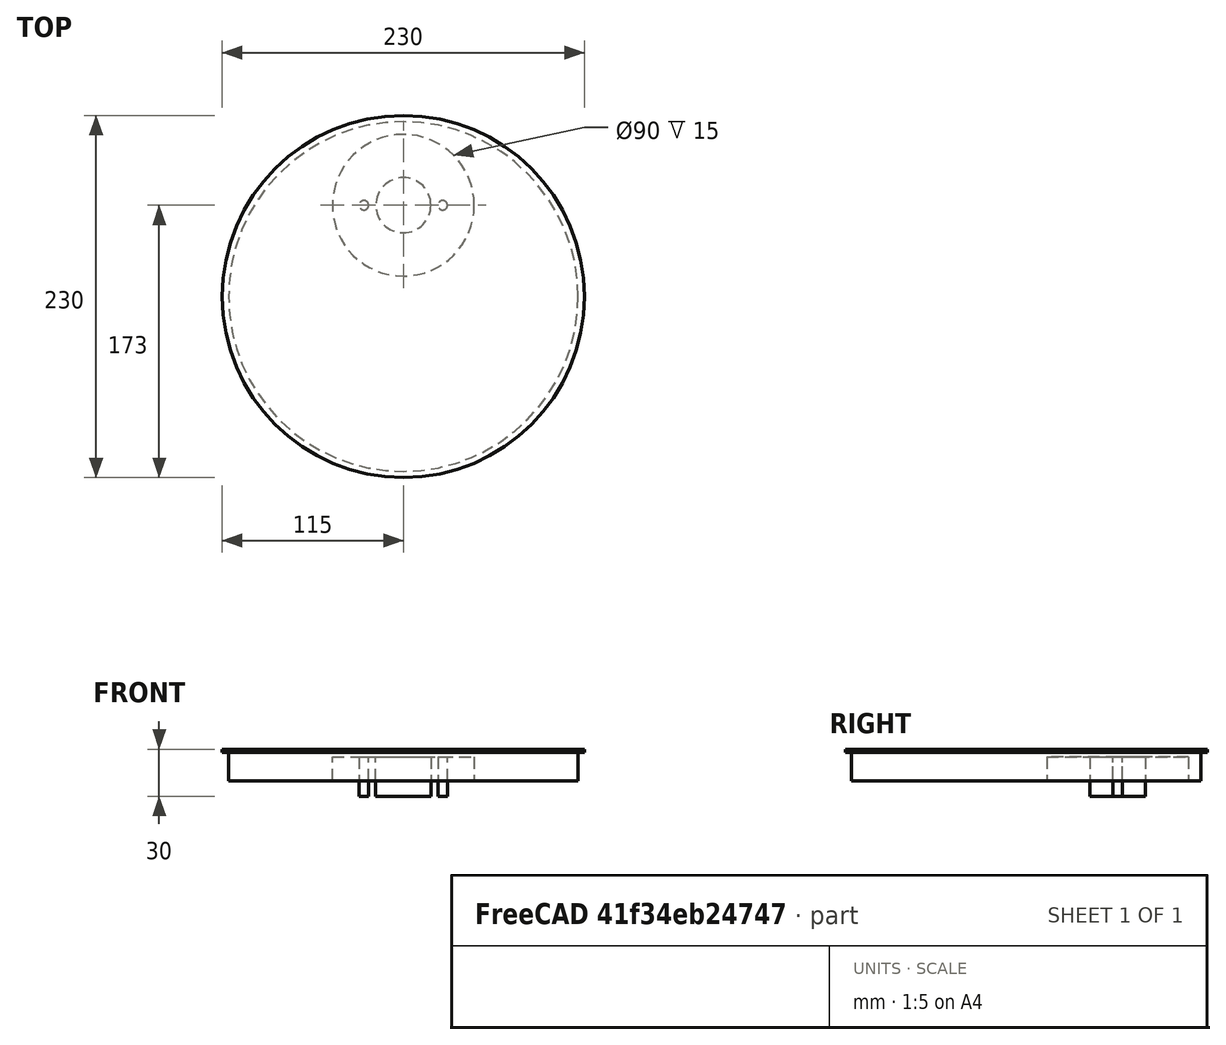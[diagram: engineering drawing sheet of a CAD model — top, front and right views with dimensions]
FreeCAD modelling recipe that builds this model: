
FCSTD DOCUMENT  (FreeCAD 0.17R13519 (Git))
Label: form
License: All rights reserved
LicenseURL: http://en.wikipedia.org/wiki/All_rights_reserved
objects: TechDraw::DrawViewDimension×11, Sketcher::SketchObject×7, PartDesign::Pocket×4, PartDesign::Body×3, PartDesign::Revolution×2, PartDesign::Pad×2, TechDraw::DrawProjGroup×2, Part::Cut×1, TechDraw::DrawSVGTemplate×1, PartDesign::FeatureBase×1, TechDraw::DrawProjGroupItem×1, TechDraw::DrawViewSection×1, TechDraw::DrawViewPart×1, TechDraw::DrawPage×1
note: 28 computed .brp shape members not serialized (recipe doc carries the construction recipe); baked Part::Feature solids carry a one-line shape summary decoded from their .brp

FEATURE [Sketcher::SketchObject] Sketch013
  MapMode = 5
  Support = -> [XY_Plane005]
  sketch-geometry (4):
    g0: LineSegment StartX=-146.596 StartY=145.589 StartZ=0 EndX=150.159 EndY=145.589 EndZ=0
    g1: LineSegment StartX=150.159 StartY=145.589 StartZ=0 EndX=150.159 EndY=-147.239 EndZ=0
    g2: LineSegment StartX=150.159 StartY=-147.239 StartZ=0 EndX=-146.596 EndY=-147.239 EndZ=0
    g3: LineSegment StartX=-146.596 StartY=-147.239 StartZ=0 EndX=-146.596 EndY=145.589 EndZ=0
  constraints (8):
    c: Coincident(g0,g1)
    c: Coincident(g1,g2)
    c: Coincident(g2,g3)
    c: Coincident(g3,g0)
    c: Horizontal(g0)
    c: Horizontal(g2)
    c: Vertical(g1)
    c: Vertical(g3)
FEATURE [Sketcher::SketchObject] Sketch014
  MapMode = 5
  Placement = pos=(0,0,0) rot=(1,0,0;1.5708rad)
  Support = -> [XZ_Plane006]
  sketch-geometry (4):
    g0: LineSegment StartX=-115 StartY=28 StartZ=0 EndX=-111 EndY=28 EndZ=0
    g1: LineSegment StartX=-111 StartY=28 StartZ=0 EndX=-111 EndY=10 EndZ=0
    g2: LineSegment StartX=-115 StartY=10 StartZ=0 EndX=-115 EndY=28 EndZ=0
    g3: LineSegment StartX=-111 StartY=10 StartZ=0 EndX=-115 EndY=10 EndZ=0
  constraints (12):
    c: Coincident(g0,g1)
    c: Coincident(g2,g0)
    c: Horizontal(g0)
    c: Vertical(g1)
    c: Vertical(g2)
    c: Distance(g0) = 4
    c: Distance(g2) = 18
    c: DistanceX(g2,g-1) = 115
    c: Coincident(g3,g1)
    c: Coincident(g3,g2)
    c: Horizontal(g3)
    c: DistanceY(g-1,g1) = 10
FEATURE [Sketcher::SketchObject] Sketch016
  MapMode = 5
  Placement = pos=(0,0,0) rot=(1,0,0;1.5708rad)
  Support = -> [XZ_Plane006]
  sketch-geometry (6):
    g0: LineSegment StartX=0 StartY=0 StartZ=0 EndX=125 EndY=0 EndZ=0
    g1: LineSegment StartX=125 StartY=30 StartZ=0 EndX=125 EndY=0 EndZ=0
    g2: LineSegment StartX=125 StartY=30 StartZ=0 EndX=115 EndY=30 EndZ=0
    g3: LineSegment StartX=115 StartY=30 StartZ=0 EndX=115 EndY=10 EndZ=0
    g4: LineSegment StartX=115 StartY=10 StartZ=0 EndX=0 EndY=10 EndZ=0
    g5: LineSegment StartX=0 StartY=10 StartZ=0 EndX=0 EndY=0 EndZ=0
  constraints (17):
    c: Coincident(g0,g-1)
    c: Horizontal(g0)
    c: Coincident(g1,g0)
    c: Coincident(g2,g1)
    c: Horizontal(g2)
    c: Coincident(g2,g3)
    c: Vertical(g3)
    c: Coincident(g3,g4)
    c: PointOnObject(g4,g-2)
    c: Horizontal(g4)
    c: Coincident(g4,g5)
    c: Coincident(g5,g-1)
    c: Vertical(g1)
    c: DistanceY(g-1,g4) = 10
    c: Distance(g2) = 10
    c: Distance(g0) = 125
    c: Distance(g1) = 30
FEATURE [PartDesign::Revolution] Revolution002
  Angle = 360
  Axis = (0,0,1)
  Base = (0,0,0)
  Placement = pos=(0,0,0) rot=(1,0,0;1.5708rad)
  Profile = -> Sketch016
  ReferenceAxis = -> Sketch016 [V_Axis]
  Reversed = true
FEATURE [Sketcher::SketchObject] Sketch015
  ExternalGeometry = -> [Revolution002]
  MapMode = 5
  Placement = pos=(0,0,10) rot=(0,0,1;3.14159rad)
  Support = -> [Revolution002]
  sketch-geometry (3):
    g0: Circle CenterX=0 CenterY=-58 CenterZ=0 NormalX=0 NormalY=0 NormalZ=1 AngleXU=0 Radius=17.5
    g1: Circle CenterX=0 CenterY=-58 CenterZ=0 NormalX=0 NormalY=0 NormalZ=1 AngleXU=0 Radius=45
    g2: GeomPoint X=1.67111 Y=-115.12 Z=0
  constraints (5):
    c: PointOnObject(g0,g-2)
    c: Radius(g0) = 17.5
    c: Coincident(g1,g0)
    c: Radius(g1) = 45
    c: DistanceY(g0,g-1) = 58
FEATURE [PartDesign::Pad] Pad006
  BaseFeature = -> Revolution002
  Length = 15
  Length2 = 100
  Placement = pos=(0,0,0) rot=(1,0,0;1.5708rad)
  Profile = -> Sketch015
  Type = 0
FEATURE [PartDesign::Pocket] Pocket005
  BaseFeature = -> Pad006
  Length = 5
  Length2 = 100
  Placement = pos=(0,0,0) rot=(1,0,0;1.5708rad)
  Profile = -> Pad006 [Face9]
  Type = 1
FEATURE [Sketcher::SketchObject] Sketch017
  ExternalGeometry = -> [Pocket005]
  MapMode = 5
  Placement = pos=(0,0,25) rot=(0,0,1;3.14159rad)
  Support = -> [Pocket005]
  sketch-geometry (3):
    g0: LineSegment [constr] StartX=-25 StartY=-58 StartZ=0 EndX=25 EndY=-58 EndZ=0
    g1: Circle CenterX=-25 CenterY=-58 CenterZ=0 NormalX=0 NormalY=0 NormalZ=1 AngleXU=0 Radius=3
    g2: Circle CenterX=25 CenterY=-58 CenterZ=0 NormalX=0 NormalY=0 NormalZ=1 AngleXU=0 Radius=3
  constraints (8):
    c: Horizontal(g0)
    c: PointOnObject(g-3,g0)
    c: Symmetric(g0,g0,g-2)
    c: DistanceX(g-1,g0) = 25
    c: Coincident(g1,g0)
    c: Coincident(g2,g0)
    c: Equal(g2,g1)
    c: Radius(g2) = 3
FEATURE [PartDesign::Pocket] Pocket006
  BaseFeature = -> Pocket005
  Length = 5
  Length2 = 100
  Placement = pos=(0,0,0) rot=(1,0,0;1.5708rad)
  Profile = -> Sketch017
  Type = 1
FEATURE [PartDesign::Revolution] Revolution003
  Angle = 360
  Axis = (0,0,1)
  Base = (0,0,0)
  BaseFeature = -> Pocket006
  Placement = pos=(0,0,0) rot=(1,0,0;1.5708rad)
  Profile = -> Sketch014
  ReferenceAxis = -> Sketch014 [V_Axis]
FEATURE [PartDesign::Pad] Pad005
  Length = 50
  Length2 = 100
  Profile = -> Sketch013
  Type = 0
FEATURE [PartDesign::Body] Body005  label="kiste"
  Group = -> [Sketch013,Pad005]
  Origin = -> Origin005
  Tip = -> Pad005
FEATURE [PartDesign::Body] Body006  label="body_clone"
  Group = -> [Sketch016,Revolution002,Sketch015,Pad006,Pocket005,Sketch017,Pocket006,Sketch014,Revolution003]
  Origin = -> Origin006
  Tip = -> Revolution003
FEATURE [Part::Cut] Cut  label="mold"
  Base = -> Body005
  Tool = -> Body006
FEATURE [TechDraw::DrawSVGTemplate] Template
  EditableTexts = Designed_by_Name=Designed by Name; Drawing_number=Drawing number; FC-Date=Date; FC-SC=Scale; FC-SH=Sheet; FC-Title=Title; Subtitle=Subtitle; Weight=Weight
  Height = 210
  Orientation = 1
  Width = 297
FEATURE [PartDesign::FeatureBase] BaseFeature
  BaseFeature = -> Cut
FEATURE [Sketcher::SketchObject] Sketch018
  ExternalGeometry = -> [BaseFeature]
  MapMode = 5
  Placement = pos=(0,0,30) rot=(1,0,0;3.14159rad)
  Support = -> [BaseFeature]
  sketch-geometry (5):
    g0: Circle CenterX=0 CenterY=0 CenterZ=0 NormalX=0 NormalY=0 NormalZ=1 AngleXU=0 Radius=115
    g1: LineSegment StartX=150.159 StartY=147.239 StartZ=0 EndX=-146.596 EndY=147.239 EndZ=0
    g2: LineSegment StartX=-146.596 StartY=147.239 StartZ=0 EndX=-146.596 EndY=-145.589 EndZ=0
    g3: LineSegment StartX=-146.596 StartY=-145.589 StartZ=0 EndX=150.159 EndY=-145.589 EndZ=0
    g4: LineSegment StartX=150.159 StartY=-145.589 StartZ=0 EndX=150.159 EndY=147.239 EndZ=0
  constraints (12):
    c: Coincident(g0,g-1)
    c: Tangent(g0,g-3)
    c: Coincident(g1,g2)
    c: Coincident(g2,g3)
    c: Coincident(g3,g4)
    c: Coincident(g4,g1)
    c: Horizontal(g1)
    c: Horizontal(g3)
    c: Vertical(g2)
    c: Vertical(g4)
    c: Coincident(g1,g-5)
    c: Coincident(g2,g-7)
FEATURE [PartDesign::Pocket] Pocket007
  BaseFeature = -> BaseFeature
  Length = 20
  Length2 = 100
  Profile = -> Sketch018
  Type = 4
FEATURE [Sketcher::SketchObject] Sketch019
  ExternalGeometry = -> [Pocket007]
  MapMode = 5
  Placement = pos=(0,0,0) rot=(1,0,0;1.5708rad)
  Support = -> [XZ_Plane007]
  sketch-geometry (4):
    g0: LineSegment StartX=-128.988 StartY=79.6118 StartZ=0 EndX=153.773 EndY=79.6118 EndZ=0
    g1: LineSegment StartX=153.773 StartY=79.6118 StartZ=0 EndX=153.773 EndY=30 EndZ=0
    g2: LineSegment StartX=153.773 StartY=30 StartZ=0 EndX=-128.988 EndY=30 EndZ=0
    g3: LineSegment StartX=-128.988 StartY=30 StartZ=0 EndX=-128.988 EndY=79.6118 EndZ=0
  constraints (9):
    c: Coincident(g0,g1)
    c: Coincident(g1,g2)
    c: Coincident(g2,g3)
    c: Coincident(g3,g0)
    c: Horizontal(g0)
    c: Horizontal(g2)
    c: Vertical(g1)
    c: Vertical(g3)
    c: PointOnObject(g-3,g2)
FEATURE [PartDesign::Pocket] Pocket008
  BaseFeature = -> Pocket007
  Length = 5
  Length2 = 100
  Midplane = true
  Profile = -> Sketch019
  Type = 1
FEATURE [PartDesign::Body] Body007
  BaseFeature = -> Cut
  Group = -> [BaseFeature,Sketch018,Pocket007,Sketch019,Pocket008]
  Origin = -> Origin007
  Tip = -> Pocket008
FEATURE [TechDraw::DrawProjGroup] ProjGroup
  AutoDistribute = true
  CubeDirs = (6) [(0,1,-6.12323e-17),(0,-6.12323e-17,-1),(-1,0,0),(0,6.12323e-17,1),(1,0,0),(0,-1,6.12323e-17)]
  CubeRotations = (6) [(1,0,0),(1,0,0),(0,6.12323e-17,-1),(-1,0,0),(0,-6.12323e-17,1),(1,0,0)]
  LockPosition = false
  ProjectionType = 0
  Rotation = 0
  ScaleType = 0
  Source = -> [Body007]
  X = -127.493
  Y = 77.4007
  spacingX = 15
  spacingY = 15
FEATURE [TechDraw::DrawProjGroupItem] ProjItem001  label="     Top"
  CoarseView = false
  Direction = (0,0,-1)
  Focus = 100
  HardHidden = false
  IsoCount = 0
  IsoHidden = false
  IsoVisible = false
  LockPosition = false
  Perspective = false
  Rotation = 0
  RotationVector = (1,0,0)
  ScaleType = 0
  SeamHidden = false
  SeamVisible = false
  SmoothHidden = false
  SmoothVisible = false
  Source = -> [Body007]
  Type = 0
  X = 0
  Y = 0
FEATURE [TechDraw::DrawProjGroup] ProjGroup001
  Anchor = -> ProjItem001
  AutoDistribute = true
  CubeDirs = (6) [(0,1,-6.12323e-17),(0,-6.12323e-17,-1),(-1,0,0),(0,6.12323e-17,1),(1,0,0),(0,-1,6.12323e-17)]
  CubeRotations = (6) [(1,0,0),(1,0,0),(0,6.12323e-17,-1),(-1,0,0),(0,-6.12323e-17,1),(1,0,0)]
  LockPosition = false
  ProjectionType = 0
  Rotation = 0
  Scale = 0.2
  ScaleType = 2
  Source = -> [Body007]
  Views = -> [ProjItem001]
  X = 243.564
  Y = 95.2891
  spacingX = 15
  spacingY = 15
FEATURE [TechDraw::DrawViewSection] Section001  label="Section A - A001"
  BaseView = -> ProjItem001
  CoarseView = false
  Direction = (1,0,0)
  Focus = 100
  HardHidden = false
  HatchScale = 1
  IsoCount = 0
  IsoHidden = false
  IsoVisible = false
  LockPosition = false
  NameGeomPattern = Diamond
  Perspective = false
  Rotation = 180
  ScaleType = 0
  SeamHidden = false
  SeamVisible = false
  SectionDirection = 1
  SectionNormal = (1,0,0)
  SectionOrigin = (0,0,15)
  SectionSymbol = A
  SmoothHidden = false
  SmoothVisible = false
  Source = -> [Body007]
  X = 154.122
  Y = 161.221
FEATURE [TechDraw::DrawViewPart] View
  CoarseView = false
  Direction = (-1,3,-2.5)
  Focus = 100
  HardHidden = false
  IsoCount = 0
  IsoHidden = false
  IsoVisible = false
  LockPosition = false
  Perspective = false
  Rotation = 180
  Scale = 0.5
  ScaleType = 0
  SeamHidden = false
  SeamVisible = false
  SmoothHidden = false
  SmoothVisible = false
  Source = -> [Body007]
  X = 78.4021
  Y = 60.8931
FEATURE [TechDraw::DrawViewDimension] Dimension
  FormatSpec = %.2f
  LockPosition = false
  MeasureType = 1
  References2D = -> [Section001]
  Rotation = 0
  ScaleType = 0
  Type = 1
  X = -1.77465
  Y = -31.9437
FEATURE [TechDraw::DrawViewDimension] Dimension001
  FormatSpec = %.2f
  LockPosition = false
  MeasureType = 1
  References2D = -> [Section001]
  Rotation = 0
  ScaleType = 0
  Type = 1
  X = -2.02113
  Y = 36.4296
FEATURE [TechDraw::DrawViewDimension] Dimension002
  FormatSpec = %.2f
  LockPosition = false
  MeasureType = 1
  References2D = -> [Section001]
  Rotation = 0
  ScaleType = 0
  Type = 2
  X = 118.632
  Y = -20.3763
FEATURE [TechDraw::DrawViewDimension] Dimension004
  FormatSpec = %.2f
  LockPosition = false
  MeasureType = 1
  References2D = -> [Section001]
  Rotation = 0
  ScaleType = 0
  Type = 1
  X = -57.4638
  Y = 21.8591
FEATURE [TechDraw::DrawViewDimension] Dimension005
  FormatSpec = %.2f
  LockPosition = false
  MeasureType = 1
  References2D = -> [Section001]
  Rotation = 0
  ScaleType = 0
  Type = 0
  X = -57.8961
  Y = 28.6879
FEATURE [TechDraw::DrawViewDimension] Dimension007
  FormatSpec = %.2f
  LockPosition = false
  MeasureType = 1
  References2D = -> [Section001]
  Rotation = 0
  ScaleType = 0
  Type = 2
  X = 126.444
  Y = -4.6831
FEATURE [TechDraw::DrawViewDimension] Dimension008
  FormatSpec = %.2f
  LockPosition = false
  MeasureType = 1
  References2D = -> [Section001]
  Rotation = 0
  ScaleType = 0
  Type = 2
  X = -137.042
  Y = 10.1056
FEATURE [TechDraw::DrawViewDimension] Dimension009
  FormatSpec = %.2f
  LockPosition = false
  MeasureType = 1
  References2D = -> [Section001]
  Rotation = 0
  ScaleType = 0
  Type = 2
  X = -47.8169
  Y = 1.97183
FEATURE [TechDraw::DrawViewDimension] Dimension010
  FormatSpec = %.2f
  LockPosition = false
  MeasureType = 1
  References2D = -> [Section001]
  Rotation = 0
  ScaleType = 0
  Type = 2
  X = -8.1338
  Y = -3.69718
FEATURE [TechDraw::DrawViewDimension] Dimension011
  FormatSpec = %.2f
  LockPosition = false
  MeasureType = 1
  References2D = -> [Section001]
  Rotation = 0
  ScaleType = 0
  Type = 2
  X = -137.042
  Y = -5.91549
FEATURE [TechDraw::DrawViewDimension] Dimension012
  FormatSpec = %.2f
  LockPosition = false
  MeasureType = 1
  References2D = -> [Section001]
  Rotation = 0
  ScaleType = 0
  Type = 1
  X = 105.164
  Y = -26.4965
FEATURE [TechDraw::DrawPage] Page
  KeepUpdated = true
  ProjectionType = 0
  Template = -> Template
  Views = -> [ProjGroup,ProjGroup001,Section001,View,Dimension,Dimension001,Dimension002,Dimension004,Dimension005,Dimension007,Dimension008,Dimension009,Dimension010,Dimension011,Dimension012]
